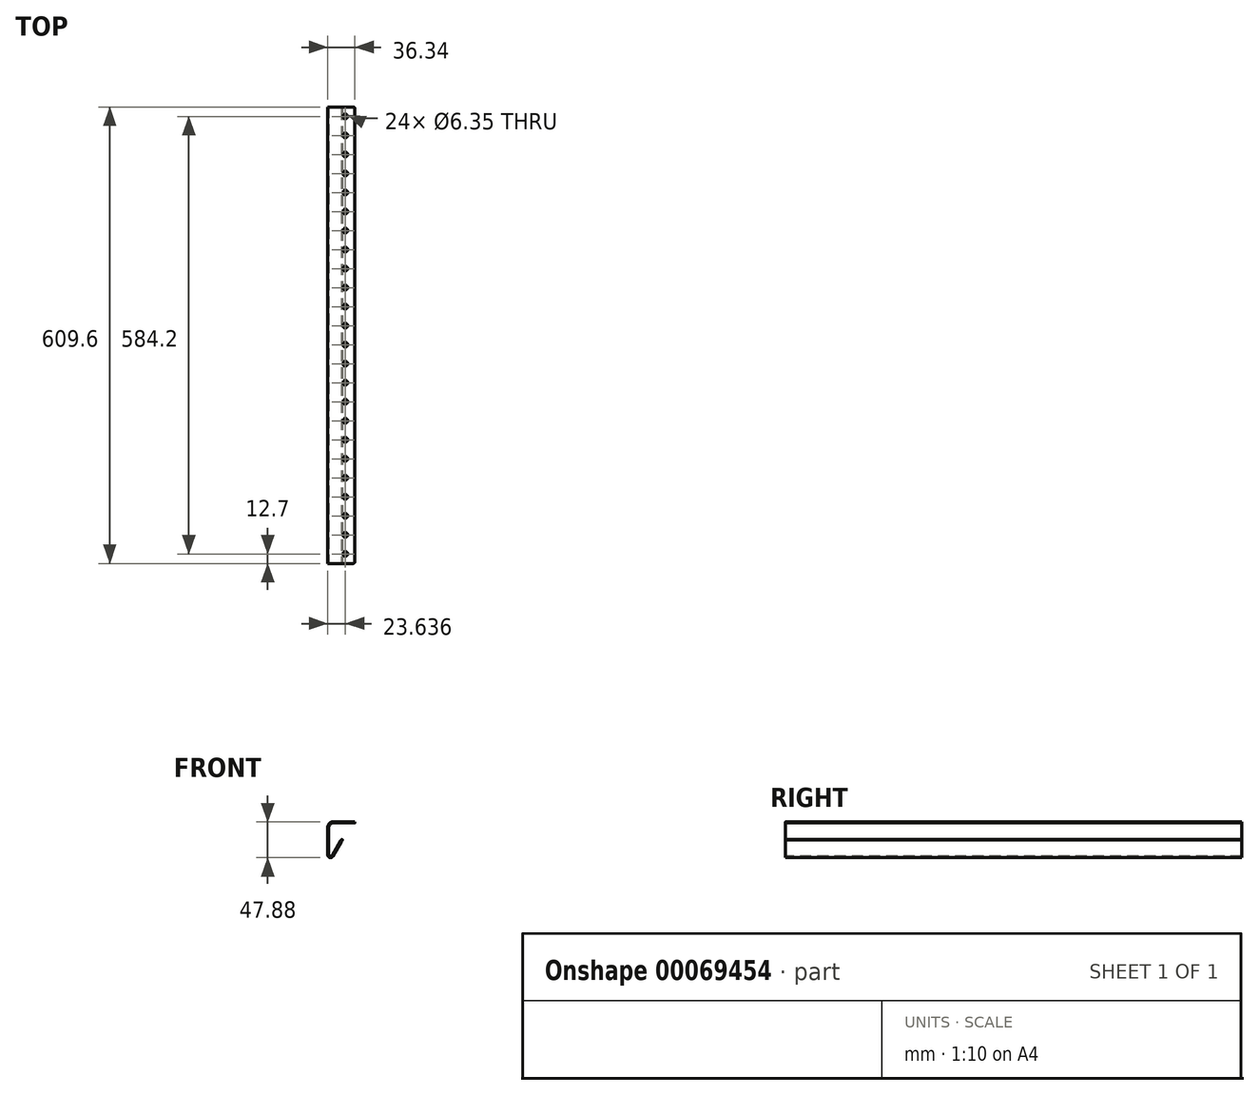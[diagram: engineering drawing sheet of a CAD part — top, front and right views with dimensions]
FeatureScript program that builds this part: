
annotation { "Feature Type Name" : "Feature", "Feature Type Description" : "" }
export const myFeature = defineFeature(function(context is Context, id is Id, definition is map)
    precondition{}
    {
        {
            var Q0;
            Q0=qCreatedBy(makeId("Front.planeOp"),FACE);
            var sketch = newSketch(context, id + "F0", { "sketchPlane" : qUnion([Q0])});
            skLineSegment(sketch, "E0", {"start": v(12.07, 19.26) * mm, "end": v(-16.42, 19.26) * mm});
            skLineSegment(sketch, "E1", {"start": v(-22.77, 12.91) * mm, "end": v(-22.77, -22.45) * mm});
            skLineSegment(sketch, "E2", {"start": v(-18.03, -23.72) * mm, "end": v(-5.76, -2.47) * mm});
            skLineSegment(sketch, "E3.0", {"start": v(-17.16, -25.21) * mm, "end": v(-4.46, -3.22) * mm});
            skLineSegment(sketch, "E3.1", {"start": v(-24.27, 13.14) * mm, "end": v(-24.27, -23.3) * mm});
            skLineSegment(sketch, "E3.2", {"start": v(12.07, 20.76) * mm, "end": v(-16.65, 20.76) * mm});
            skLineSegment(sketch, "E4", {"start": v(-4.46, -3.22) * mm, "end": v(-5.76, -2.47) * mm});
            skLineSegment(sketch, "E5", {"start": v(12.07, 20.76) * mm, "end": v(12.07, 19.26) * mm});
            skPoint(sketch, "E6.visualSharp", {"position": v(-22.77, 19.26) * mm});
            skArc(sketch, "E6.filletArc", {"start": v(-16.42, 19.26) * mm, "mid": v(-20.91, 17.4) * mm, "end": v(-22.77, 12.91) * mm});
            skPoint(sketch, "E7.visualSharp", {"position": v(-22.77, -31.93) * mm});
            skArc(sketch, "E7.filletArc", {"start": v(-22.77, -22.45) * mm, "mid": v(-20.9, -24.9) * mm, "end": v(-18.03, -23.72) * mm});
            skPoint(sketch, "E8.visualSharp", {"position": v(-24.27, -37.53) * mm});
            skArc(sketch, "E8.filletArc", {"start": v(-24.27, -23.3) * mm, "mid": v(-21.45, -26.99) * mm, "end": v(-17.16, -25.21) * mm});
            skPoint(sketch, "E9.visualSharp", {"position": v(-24.27, 20.76) * mm});
            skArc(sketch, "E9.filletArc", {"start": v(-16.65, 20.76) * mm, "mid": v(-22.04, 18.53) * mm, "end": v(-24.27, 13.14) * mm});
            skSolve(sketch);
        }
        {
            var Q0;
            Q0 = qSketchRegion(id + "F0", true);
            extrude(context, id + "F1", {"entities" : qUnion([Q0]), "oppositeDirection" : true, "depth" : 609.6 * mm});
        }
        {
            var Q0;
            Q0=makeQuery(id+"F1.opExtrude","SWEPT_FACE",FACE,{"disambiguationData":[OSD([sQuery(id+"F0.wireOp",EDGE,"E3.2")])]});
            var sketch = newSketch(context, id + "F2", { "sketchPlane" : qUnion([Q0])});
            skCircle(sketch, "E10", {"center": v(-0.63, 12.7) * mm, "radius": 3.18 * mm});
            skCircle(sketch, "E11.0.1.0", {"center": v(-0.63, 38.1) * mm, "radius": 3.18 * mm});
            skCircle(sketch, "E11.0.2.0", {"center": v(-0.63, 63.5) * mm, "radius": 3.18 * mm});
            skCircle(sketch, "E11.0.3.0", {"center": v(-0.63, 88.9) * mm, "radius": 3.18 * mm});
            skCircle(sketch, "E11.0.4.0", {"center": v(-0.63, 114.3) * mm, "radius": 3.18 * mm});
            skCircle(sketch, "E11.0.5.0", {"center": v(-0.63, 139.7) * mm, "radius": 3.18 * mm});
            skCircle(sketch, "E11.0.6.0", {"center": v(-0.63, 165.1) * mm, "radius": 3.18 * mm});
            skCircle(sketch, "E11.0.7.0", {"center": v(-0.63, 190.5) * mm, "radius": 3.18 * mm});
            skCircle(sketch, "E11.0.8.0", {"center": v(-0.63, 215.9) * mm, "radius": 3.18 * mm});
            skCircle(sketch, "E11.0.9.0", {"center": v(-0.63, 241.3) * mm, "radius": 3.18 * mm});
            skCircle(sketch, "E11.0.10.0", {"center": v(-0.63, 266.7) * mm, "radius": 3.18 * mm});
            skCircle(sketch, "E11.0.11.0", {"center": v(-0.63, 292.1) * mm, "radius": 3.18 * mm});
            skCircle(sketch, "E11.0.12.0", {"center": v(-0.63, 317.5) * mm, "radius": 3.18 * mm});
            skCircle(sketch, "E11.0.13.0", {"center": v(-0.63, 342.9) * mm, "radius": 3.18 * mm});
            skCircle(sketch, "E11.0.14.0", {"center": v(-0.63, 368.3) * mm, "radius": 3.18 * mm});
            skCircle(sketch, "E11.0.15.0", {"center": v(-0.63, 393.7) * mm, "radius": 3.18 * mm});
            skCircle(sketch, "E11.0.16.0", {"center": v(-0.63, 419.1) * mm, "radius": 3.18 * mm});
            skCircle(sketch, "E11.0.17.0", {"center": v(-0.63, 444.5) * mm, "radius": 3.18 * mm});
            skLineSegment(sketch, "E11.direction1", {"start": v(-0.63, 12.7) * mm, "end": v(24.77, 12.7) * mm, "construction": true});
            skLineSegment(sketch, "E11.direction2", {"start": v(-0.63, 12.7) * mm, "end": v(-0.63, 38.1) * mm, "construction": true});
            skCircle(sketch, "E12.0.0.18", {"center": v(-0.63, 469.9) * mm, "radius": 3.18 * mm});
            skCircle(sketch, "E12.0.0.19", {"center": v(-0.63, 495.3) * mm, "radius": 3.18 * mm});
            skCircle(sketch, "E12.0.0.20", {"center": v(-0.63, 520.7) * mm, "radius": 3.18 * mm});
            skCircle(sketch, "E12.0.0.21", {"center": v(-0.63, 546.1) * mm, "radius": 3.18 * mm});
            skCircle(sketch, "E12.0.0.22", {"center": v(-0.63, 571.5) * mm, "radius": 3.18 * mm});
            skCircle(sketch, "E12.0.0.23", {"center": v(-0.63, 596.9) * mm, "radius": 3.18 * mm});
            skSolve(sketch);
        }
        {
            var Q0;
            Q0 = qSketchRegion(id + "F2", true);
            extrude(context, id + "F3", {"entities" : qUnion([Q0]), "operationType" : NewBodyOperationType.REMOVE, "oppositeDirection" : true, "depth" : 25.4 * mm});
        }
        {
            var Q0;
            Q0=makeQuery(id+"F1.opExtrude","CAP_EDGE",EDGE,{"disambiguationData":[OSD([sQuery(id+"F0.wireOp",EDGE,"E5")])],"isStart":true});
            var Q1;
            Q1=makeQuery(id+"F1.opExtrude","CAP_EDGE",EDGE,{"disambiguationData":[OSD([sQuery(id+"F0.wireOp",EDGE,"E4")])],"isStart":true});
            var Q2;
            Q2=makeQuery(id+"F1.opExtrude","CAP_EDGE",EDGE,{"disambiguationData":[OSD([sQuery(id+"F0.wireOp",EDGE,"E4")])],"isStart":false});
            var Q3;
            Q3=makeQuery(id+"F1.opExtrude","CAP_EDGE",EDGE,{"disambiguationData":[OSD([sQuery(id+"F0.wireOp",EDGE,"E5")])],"isStart":false});
            fillet(context, id + "F4", {"entities" : qUnion([Q0, Q1, Q2, Q3]), "radius" : 2.54 * mm, "tangentPropagation" : true, "allowEdgeOverflow" : false});
        }
    });
